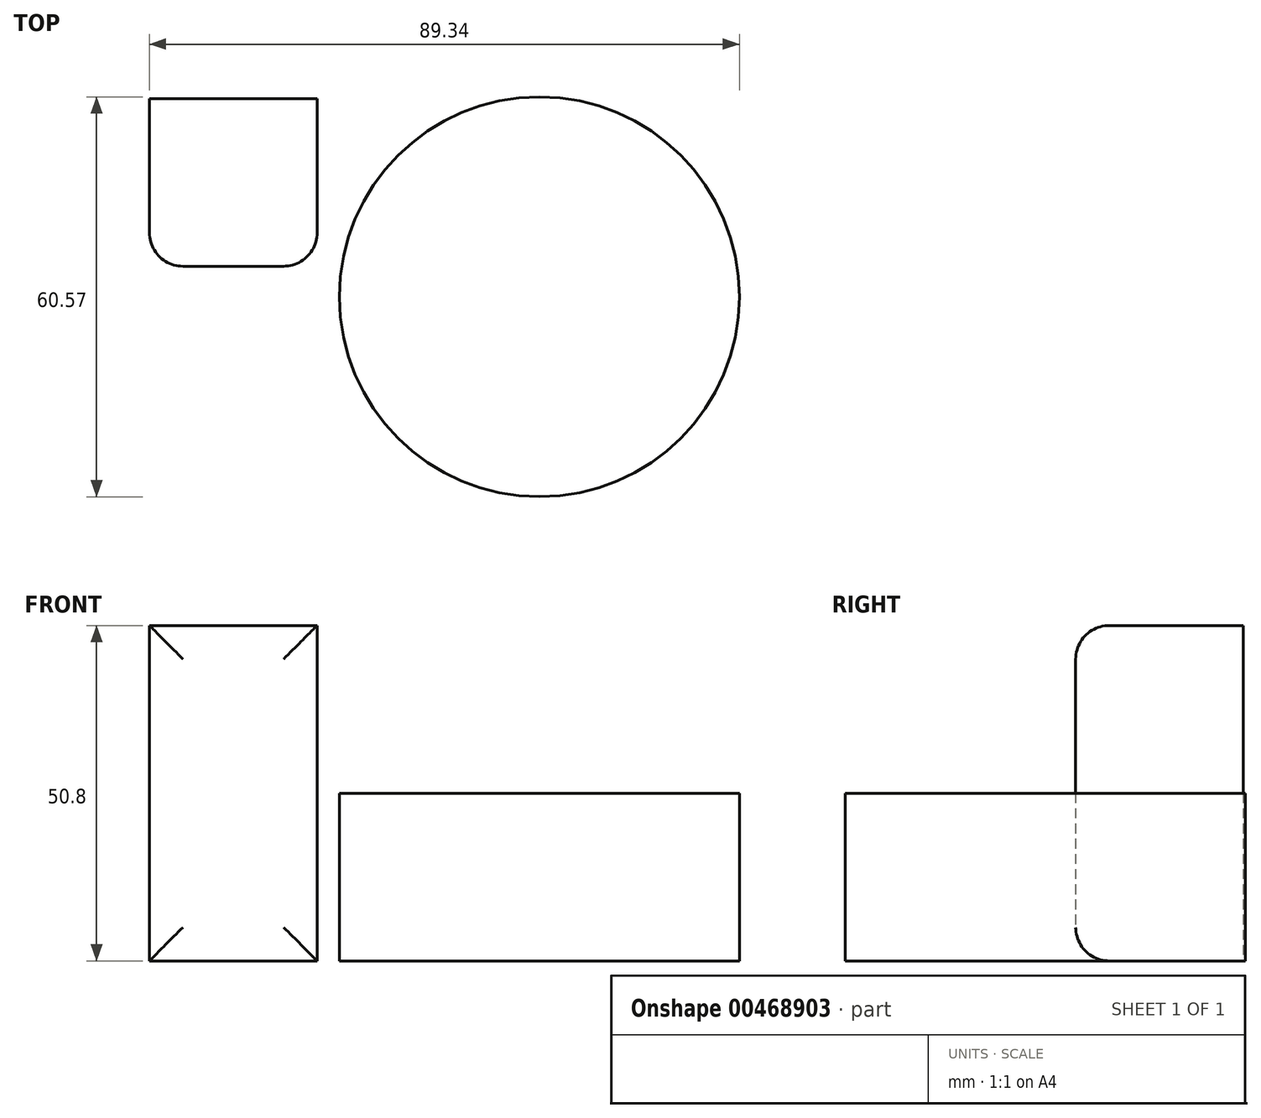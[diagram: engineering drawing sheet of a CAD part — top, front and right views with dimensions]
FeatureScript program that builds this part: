
annotation { "Feature Type Name" : "Feature", "Feature Type Description" : "" }
export const myFeature = defineFeature(function(context is Context, id is Id, definition is map)
    precondition{}
    {
        {
            var Q0;
            Q0=qCreatedBy(makeId("Top.planeOp"),FACE);
            var sketch = newSketch(context, id + "F0", { "sketchPlane" : qUnion([Q0])});
            skLineSegment(sketch, "E0.bottom", {"start": v(0, 0) * mm, "end": v(25.4, 0) * mm});
            skLineSegment(sketch, "E0.top", {"start": v(0, 25.4) * mm, "end": v(25.4, 25.4) * mm});
            skLineSegment(sketch, "E0.left", {"start": v(0, 0) * mm, "end": v(0, 25.4) * mm});
            skLineSegment(sketch, "E0.right", {"start": v(25.4, 0) * mm, "end": v(25.4, 25.4) * mm});
            skSolve(sketch);
        }
        {
            var Q0;
            Q0 = qSketchRegion(id + "F0", true);
            extrude(context, id + "F1", {"entities" : qUnion([Q0]), "depth" : 50.8 * mm, "offsetDistance" : 25.4 * mm});
        }
        {
            var Q0;
            Q0=makeQuery(id+"F1.opExtrude","SWEPT_FACE",FACE,{"disambiguationData":[OSD([sQuery(id+"F0.wireOp",EDGE,"E0.bottom")])]});
            fillet(context, id + "F2", {"entities" : qUnion([Q0]), "tangentPropagation" : true, "radius" : 5.08 * mm, "defaultsChanged" : false, "vertexSettings" : [], "allowEdgeOverflow" : false});
        }
        {
            var Q0;
            Q0=qCreatedBy(makeId("Top.planeOp"),FACE);
            var sketch = newSketch(context, id + "F3", { "sketchPlane" : qUnion([Q0])});
            skCircle(sketch, "E1", {"center": v(59.06, -4.62) * mm, "radius": 30.28 * mm});
            skSolve(sketch);
        }
        {
            var Q0;
            Q0=makeQuery(id+"F3.imprint","IMPRINT",FACE,{"disambiguationData":[TD([[makeQuery(id+"F3.imprint","IMPRINT",EDGE,{"derivedFrom":sQuery(id+"F3.wireOp",EDGE,"E1")}),1.0]])]});
            extrude(context, id + "F4", {"entities" : qUnion([Q0]), "depth" : 25.4 * mm, "offsetDistance" : 25.4 * mm});
        }
    });
